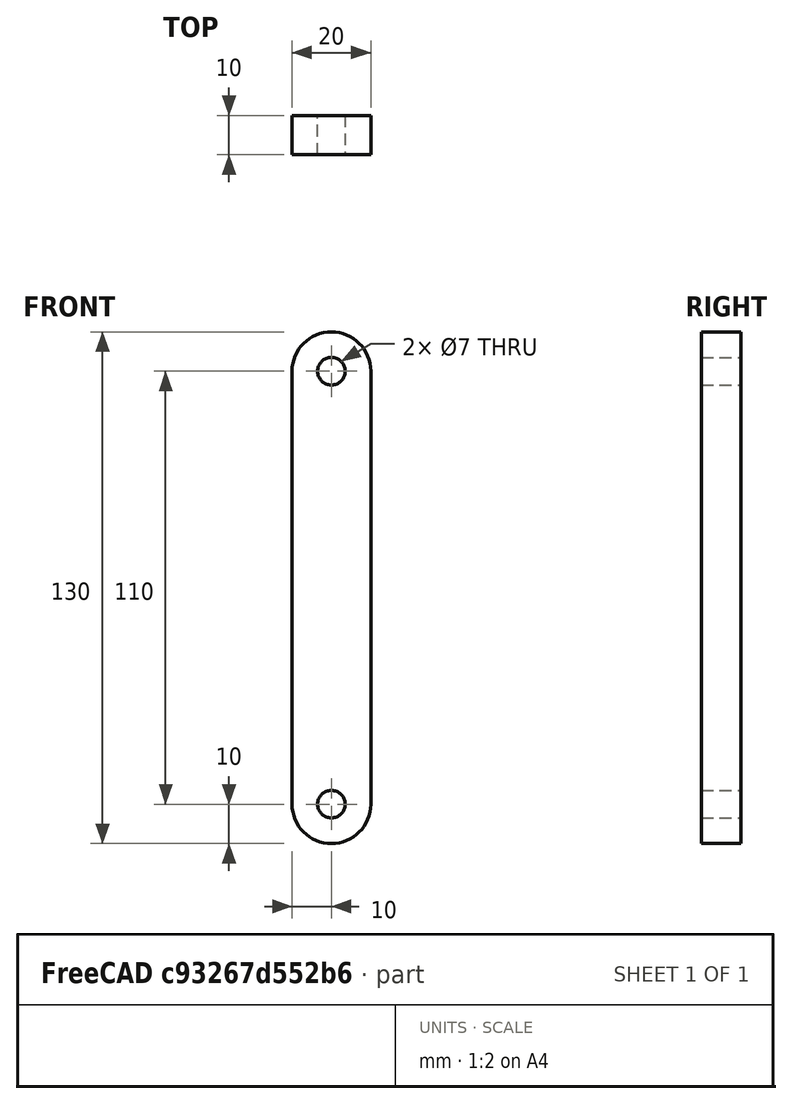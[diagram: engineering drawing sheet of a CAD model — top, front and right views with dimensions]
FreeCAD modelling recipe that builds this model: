
FCSTD DOCUMENT  (FreeCAD 1.2R20260127 (Git shallow))
Label: 002_LinkBody
License: All rights reserved
LicenseURL: http://en.wikipedia.org/wiki/All_rights_reserved
objects: Sketcher::SketchObject×2, App::Point×1, PartDesign::SubShapeBinder×1, PartDesign::Pad×1, PartDesign::Body×1
note: 9 computed .brp shape members not serialized (recipe doc carries the construction recipe); baked Part::Feature solids carry a one-line shape summary decoded from their .brp

FEATURE [Sketcher::SketchObject] Sketch  label="Mastersketch"
  ArcFitTolerance = 1e-06
  AttachmentSupport = -> [XZ_Plane]
  ExternalTypes = [0]
  FullyConstrained = true
  MakeInternals = false
  MapMode = 5
  Placement = pos=(0,0,0) rot=(1,0,0;1.5708rad)
  sketch-geometry (19):
    g0: ArcOfCircle CenterX=2e-16 CenterY=55 CenterZ=0 NormalX=0 NormalY=0 NormalZ=1 AngleXU=0 Radius=10 StartAngle=4e-16 EndAngle=3.14159
    g1: ArcOfCircle CenterX=-2e-16 CenterY=-55 CenterZ=0 NormalX=0 NormalY=0 NormalZ=1 AngleXU=0 Radius=10 StartAngle=3.14159 EndAngle=6.28319
    g2: LineSegment StartX=10 StartY=55 StartZ=0 EndX=10 EndY=-55 EndZ=0
    g3: LineSegment StartX=-10 StartY=55 StartZ=0 EndX=-10 EndY=-55 EndZ=0
    g4: ArcOfCircle CenterX=0 CenterY=-25 CenterZ=0 NormalX=0 NormalY=0 NormalZ=1 AngleXU=0 Radius=25 StartAngle=6.01325 EndAngle=9.69471
    g5: ArcOfCircle CenterX=-2e-16 CenterY=-55 CenterZ=0 NormalX=0 NormalY=0 NormalZ=1 AngleXU=0 Radius=17 StartAngle=3.41153 EndAngle=6.01325
    g6: LineSegment StartX=24.0947 StartY=-31.6667 StartZ=0 EndX=16.3844 EndY=-59.5333 EndZ=0
    g7: LineSegment StartX=-16.3844 StartY=-59.5333 StartZ=0 EndX=-24.0947 EndY=-31.6667 EndZ=0
    g8: Circle CenterX=2e-16 CenterY=55 CenterZ=0 NormalX=0 NormalY=0 NormalZ=1 AngleXU=0 Radius=3.5
    g9: Circle CenterX=-2e-16 CenterY=-55 CenterZ=0 NormalX=0 NormalY=0 NormalZ=1 AngleXU=0 Radius=3.5
    g10: LineSegment StartX=-30 StartY=80 StartZ=0 EndX=-30 EndY=20 EndZ=0
    g11: LineSegment StartX=-30 StartY=20 StartZ=0 EndX=30 EndY=20 EndZ=0
    g12: LineSegment StartX=30 StartY=20 StartZ=0 EndX=30 EndY=80 EndZ=0
    g13: LineSegment StartX=30 StartY=80 StartZ=0 EndX=-30 EndY=80 EndZ=0
    g14: ArcOfCircle CenterX=0 CenterY=-40 CenterZ=0 NormalX=0 NormalY=0 NormalZ=1 AngleXU=0 Radius=10 StartAngle=3e-16 EndAngle=3.14159
    g15: LineSegment StartX=10 StartY=-40 StartZ=0 EndX=10 EndY=-100 EndZ=0
    g16: LineSegment StartX=-10 StartY=-40 StartZ=0 EndX=-10 EndY=-100 EndZ=0
    g17: LineSegment StartX=-10 StartY=-100 StartZ=0 EndX=10 EndY=-100 EndZ=0
    g18: Circle CenterX=0 CenterY=-40 CenterZ=0 NormalX=0 NormalY=0 NormalZ=1 AngleXU=0 Radius=3.5
  constraints (46):
    c: Tangent(g0,g2) = 1.5708
    c: Tangent(g0,g3) = -1.5708
    c: Tangent(g1,g2) = 1.5708
    c: Tangent(g1,g3) = -1.5708
    c: Equal(g0,g1)
    c: Vertical(g2)
    c: Radius(g0) = 10
    c: DistanceY(g1,g0) = 110
    c: Symmetric(g0,g1,g-1)
    c: PointOnObject(g4,g-2)
    c: Coincident(g1,g5)
    c: Radius(g4) = 25
    c: Radius(g5) = 17
    c: Tangent(g7,g4) = 1.5708
    c: Tangent(g7,g5) = 1.5708
    c: Tangent(g6,g5) = 1.5708
    c: Tangent(g6,g4) = 1.5708
    c: DistanceY(g1,g4) = 30
    c: Coincident(g8,g0)
    c: Coincident(g9,g1)
    c: Diameter(g8) = 7
    c: Coincident(g10,g11)
    c: Coincident(g11,g12)
    c: Coincident(g12,g13)
    c: Coincident(g13,g10)
    c: Vertical(g10)
    c: Vertical(g12)
    c: Horizontal(g11)
    c: DistanceX(g13,g13) = 60
    c: Equal(g13,g10)
    c: Symmetric(g12,g10,g-2)
    c: DistanceY(g-1,g10) = 20
    c: Tangent(g14,g15) = 1.5708
    c: Tangent(g14,g16) = -1.5708
    c: Vertical(g15)
    c: Coincident(g17,g16)
    c: Coincident(g17,g15)
    c: Horizontal(g17)
    c: Equal(g14,g1)
    c: Vertical(g16)
    c: DistanceY(g16,g14) = 60
    c: PointOnObject(g14,g-2)
    c: DistanceY(g14,g4) = 15
    c: Coincident(g18,g14)
    c: Equal(g18,g9)
    c: Equal(g18,g8)
FEATURE [App::Point] Origin001
  Role = Origin
FEATURE [PartDesign::SubShapeBinder] Binder
  BindCopyOnChange = 0
  BindMode = 0
  ClaimChildren = false
  Context = -> Body [Binder.]
  Fuse = false
  MakeFace = false
  OffsetFill = false
  OffsetIntersection = false
  OffsetJoinType = 0
  OffsetOpenResult = false
  PartialLoad = false
  Refine = true
  Relative = true
  Support = -> [Sketch]
  _Version = 2
FEATURE [Sketcher::SketchObject] Sketch001
  ArcFitTolerance = 1e-06
  AttachmentSupport = -> [Origin]
  ExternalGeometry = -> [Binder]
  ExternalTypes = [0,0,0,0,0,0]
  FullyConstrained = true
  MakeInternals = false
  MapMode = 5
  Placement = pos=(0,0,0) rot=(1,0,0;1.5708rad)
FEATURE [PartDesign::Pad] Pad
  Direction = (0,-1,0)
  Length = 10
  Length2 = 10
  Profile = -> Sketch001
  ReferenceAxis = -> Sketch001 [N_Axis]
  Refine = true
  SideType = 2
  Suppressed = false
  Type = 0
  Type2 = 0
FEATURE [PartDesign::Body] Body
  AllowCompound = true
  Group = -> [Binder,Sketch001,Pad]
  Origin = -> Origin
  Tip = -> Pad
